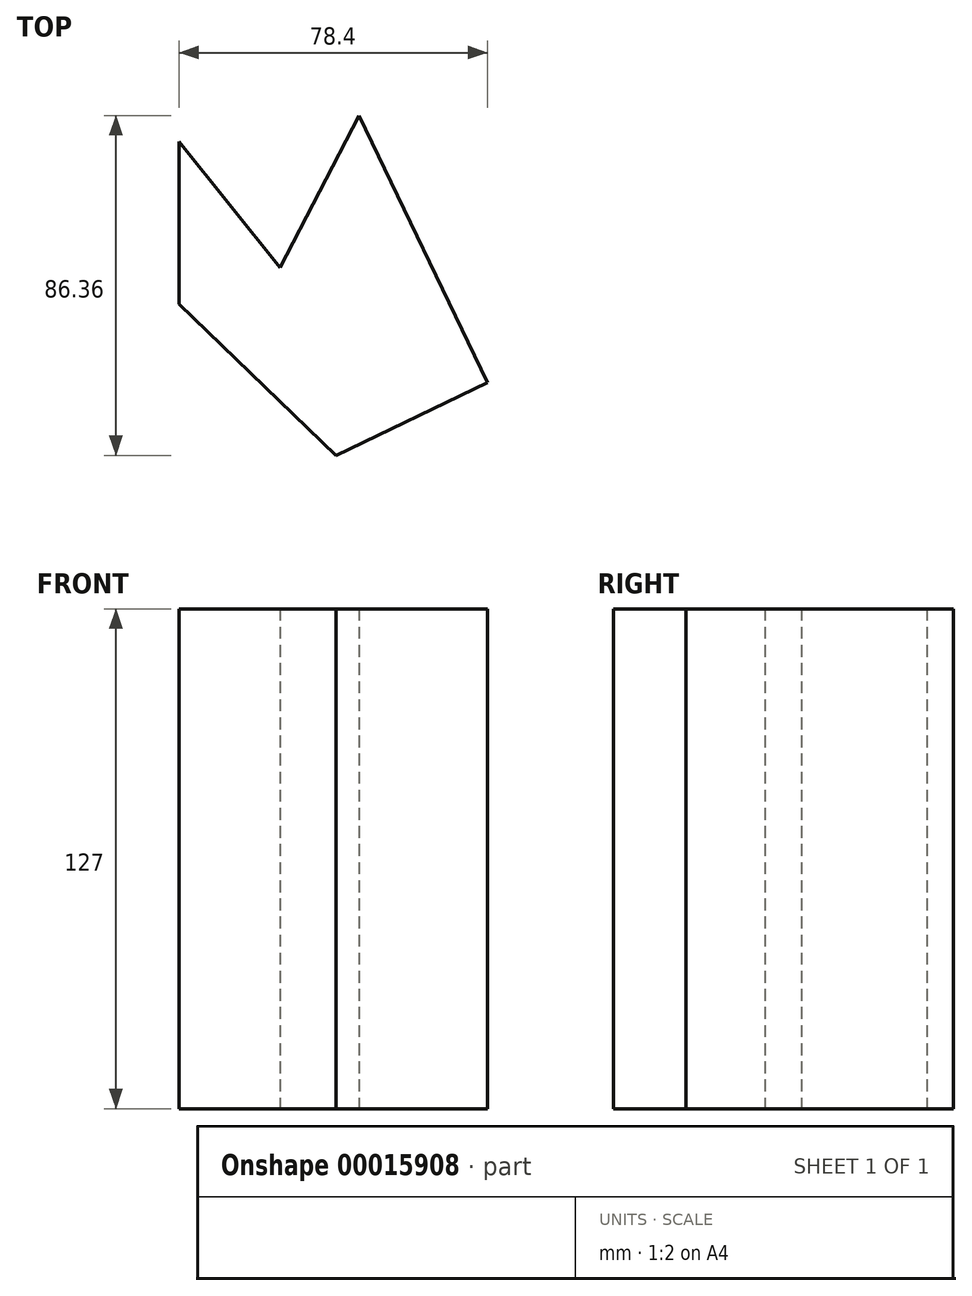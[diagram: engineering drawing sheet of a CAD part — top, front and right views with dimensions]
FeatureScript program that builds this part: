
annotation { "Feature Type Name" : "Feature", "Feature Type Description" : "" }
export const myFeature = defineFeature(function(context is Context, id is Id, definition is map)
    precondition{}
    {
        {
            var Q0;
            Q0=qCreatedBy(makeId("Top.planeOp"),FACE);
            var sketch = newSketch(context, id + "F0", { "sketchPlane" : qUnion([Q0])});
            skLineSegment(sketch, "E0", {"start": v(0, 0) * mm, "end": v(20.05, 38.62) * mm});
            skLineSegment(sketch, "E1", {"start": v(20.05, 38.62) * mm, "end": v(52.63, -29.3) * mm});
            skLineSegment(sketch, "E2", {"start": v(52.63, -29.3) * mm, "end": v(14.2, -47.74) * mm});
            skLineSegment(sketch, "E3", {"start": v(14.2, -47.74) * mm, "end": v(-25.77, -9.27) * mm});
            skLineSegment(sketch, "E4", {"start": v(-25.77, -9.27) * mm, "end": v(-25.77, 31.93) * mm});
            skLineSegment(sketch, "E5", {"start": v(-25.77, 31.93) * mm, "end": v(0, 0) * mm});
            skSolve(sketch);
        }
        {
            var Q0;
            Q0=makeQuery(id+"F0.imprint","IMPRINT",FACE,{"disambiguationData":[TD([[makeQuery(id+"F0.imprint","IMPRINT",EDGE,{"derivedFrom":sQuery(id+"F0.wireOp",EDGE,"E0")}),-1.0]])]});
            extrude(context, id + "F1", {"entities" : qUnion([Q0]), "depth" : 127 * mm});
        }
    });
